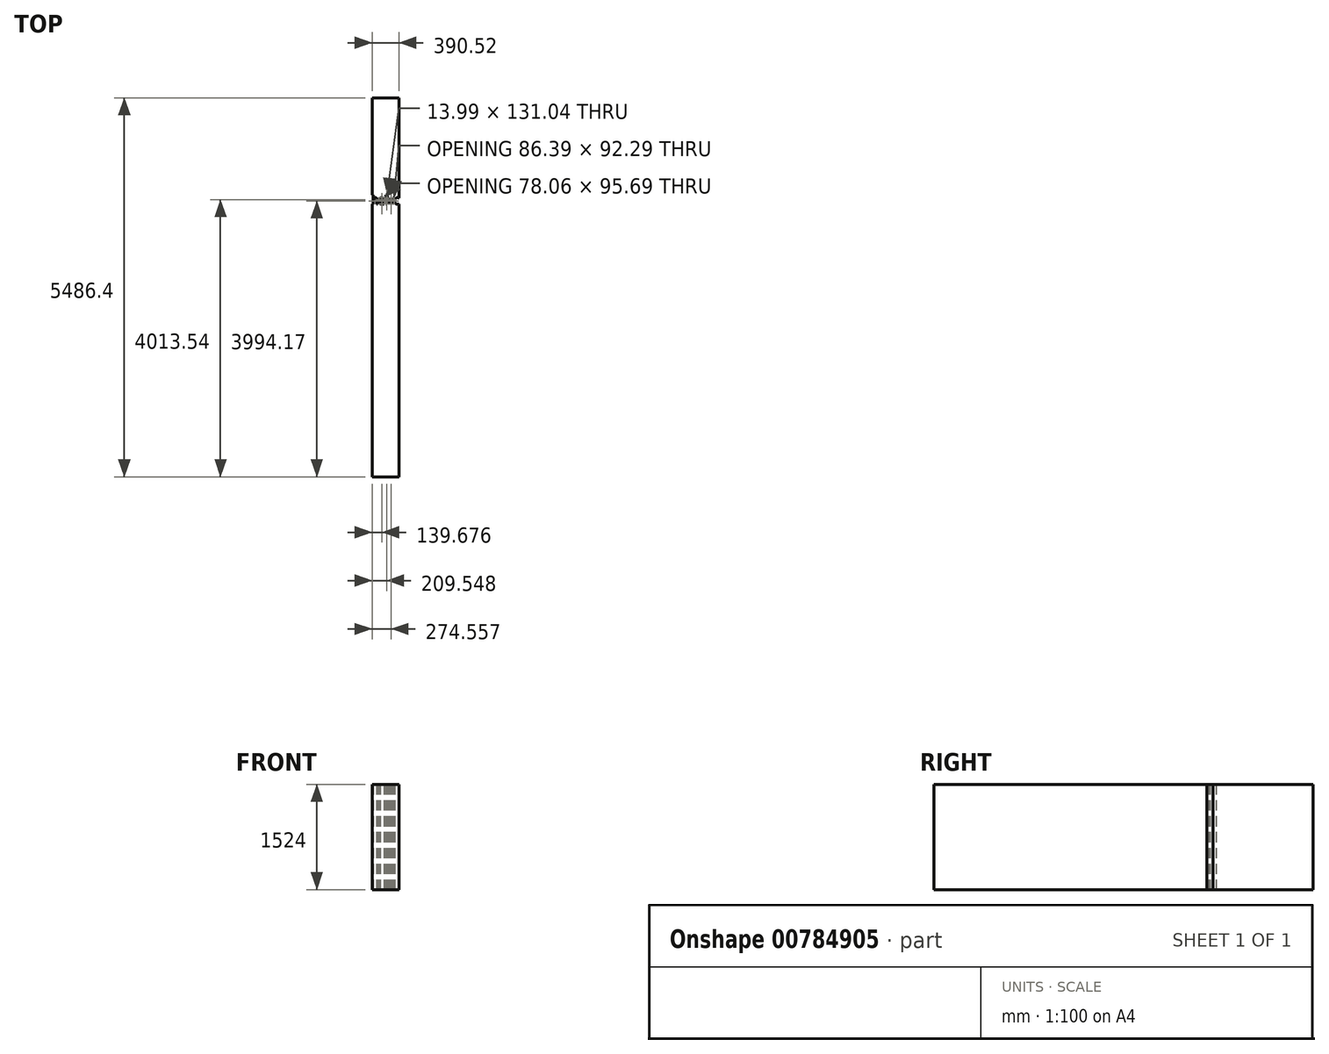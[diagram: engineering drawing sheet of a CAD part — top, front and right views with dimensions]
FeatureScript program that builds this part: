
annotation { "Feature Type Name" : "Feature", "Feature Type Description" : "" }
export const myFeature = defineFeature(function(context is Context, id is Id, definition is map)
    precondition{}
    {
        {
            var Q0;
            Q0=qCreatedBy(makeId("Top.planeOp"),FACE);
            var sketch = newSketch(context, id + "F0", { "sketchPlane" : qUnion([Q0])});
            skLineSegment(sketch, "E0.bottom", {"start": v(195.26, 2743.2) * mm, "end": v(-195.26, 2743.2) * mm});
            skLineSegment(sketch, "E0.top", {"start": v(195.26, -2743.2) * mm, "end": v(-195.26, -2743.2) * mm});
            skLineSegment(sketch, "E0.left", {"start": v(195.26, 2743.2) * mm, "end": v(195.26, -2743.2) * mm});
            skLineSegment(sketch, "E0.right", {"start": v(-195.26, 2743.2) * mm, "end": v(-195.26, -2743.2) * mm});
            skPoint(sketch, "E0.middle", {"position": v(0, 0) * mm});
            skText(sketch, "E1", { "text": "Shelves", "fontName": "OpenSans-Regular.ttf"});
            const initialGuessF0  = {"E1": [-0.3048, 1.20482, 1, 0, 0.12417]};
            skSetInitialGuess(sketch, initialGuessF0);
            skSolve(sketch);
        }
        {
            var Q0;
            Q0=makeQuery(id+"F0.imprint","IMPRINT",FACE,{"disambiguationData":[TD([[makeQuery(id+"F0.imprint","IMPRINT",EDGE,{"derivedFrom":sQuery(id+"F0.wireOp",EDGE,"E0.bottom")}),1.0]])]});
            extrude(context, id + "F1", {"entities" : qUnion([Q0]), "depth" : 1524 * mm, "offsetDistance" : 25.4 * mm});
        }
    });
